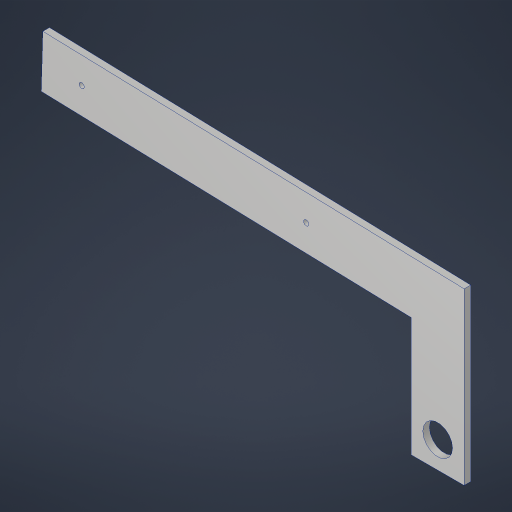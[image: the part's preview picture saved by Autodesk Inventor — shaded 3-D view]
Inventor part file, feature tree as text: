
AUTODESK INVENTOR PART (.ipt)
format: ipt  version: 2023.4 (Build 274418000, 418)  size: 192,512 bytes
history: native  units: in
note: dims shown in document units (in); Inventor stores cm internally (conversion verified against a paired STEP export)
features: sketch x1, extrude x1, hole x1
ambient origin geometry x8: Origin, YZ Plane, XZ Plane, XY Plane, X Axis, Y Axis, Z Axis, Center Point
bodies: Solid1 (feature_tree)
feature tree (3):
  sketch  "Sketch1"  dims[d0=16.0in d1=2.0in d2=1.125in d3=1.125in d4=7.375in d5=24.0in d6=8.5in d7=0.25in d10=1.125in d11=1.0in d12=0.25in d13=0.0in d14=0.201in d15=0.75in d16=0.385in d17=0.25in d18=0.5635in d19=1.0in d20=0.8108in d21=2.0in d22=1.0in d23=1.5in d24=4.5in d25=2.0in]
  extrude  "Extrusion1"  Depth=2.0in
  hole  "Hole1"  [1 undecoded]
note: 1 required parameter value undecoded (feature->parameter linkage not recoverable at this tier; creation-order binding heuristic only, values carry confidence <= 0.55)
